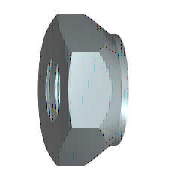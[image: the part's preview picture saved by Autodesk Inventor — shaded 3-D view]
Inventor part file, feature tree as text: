
AUTODESK INVENTOR PART (.ipt)
format: ipt  version: 2017 (Build 210142000, 142)  size: 184,832 bytes
history: native  units: mm (DEFAULTED — no unit token found)
features: sketch x3, hole x1, chamfer x1, other x1, plane x1
ambient origin geometry x7: Origin, YZ Plane, XZ Plane, X Axis, Y Axis, Z Axis, Center Point
bodies: Solid1 (feature_tree), Body (feature_tree)
feature tree (7):
  hole  "Thread"  [1 undecoded]
  chamfer  "Chamfer3"  Distance=7.0mm
  other  "Work Axis1"
  plane  "Work Plane1"
  sketch  "Sketch1"  dims[d0=8.082904mm d1=4.0mm]
  sketch  "Sketch3"  dims[d3=30.0deg d5=7.0mm d6=5.95mm d7=90.0deg d8=8.726646mm d9=1.9mm d24=3.242mm d25=6.0mm d26=4.0mm d27=2.0mm d28=14.3117mm d29=8.0mm d30=20.594885mm d10=0.378886mm d11=30.0deg d12=0.378886mm d13=30.0deg d14=0.0mm d38=0.0mm d39=0.378886mm d40=0.378886mm d41=0.0mm d42=0.0mm]
  sketch  "Sketch2"  dims[d2=0.0mm]
note: 1 required parameter value undecoded (feature->parameter linkage not recoverable at this tier; creation-order binding heuristic only, values carry confidence <= 0.55)
